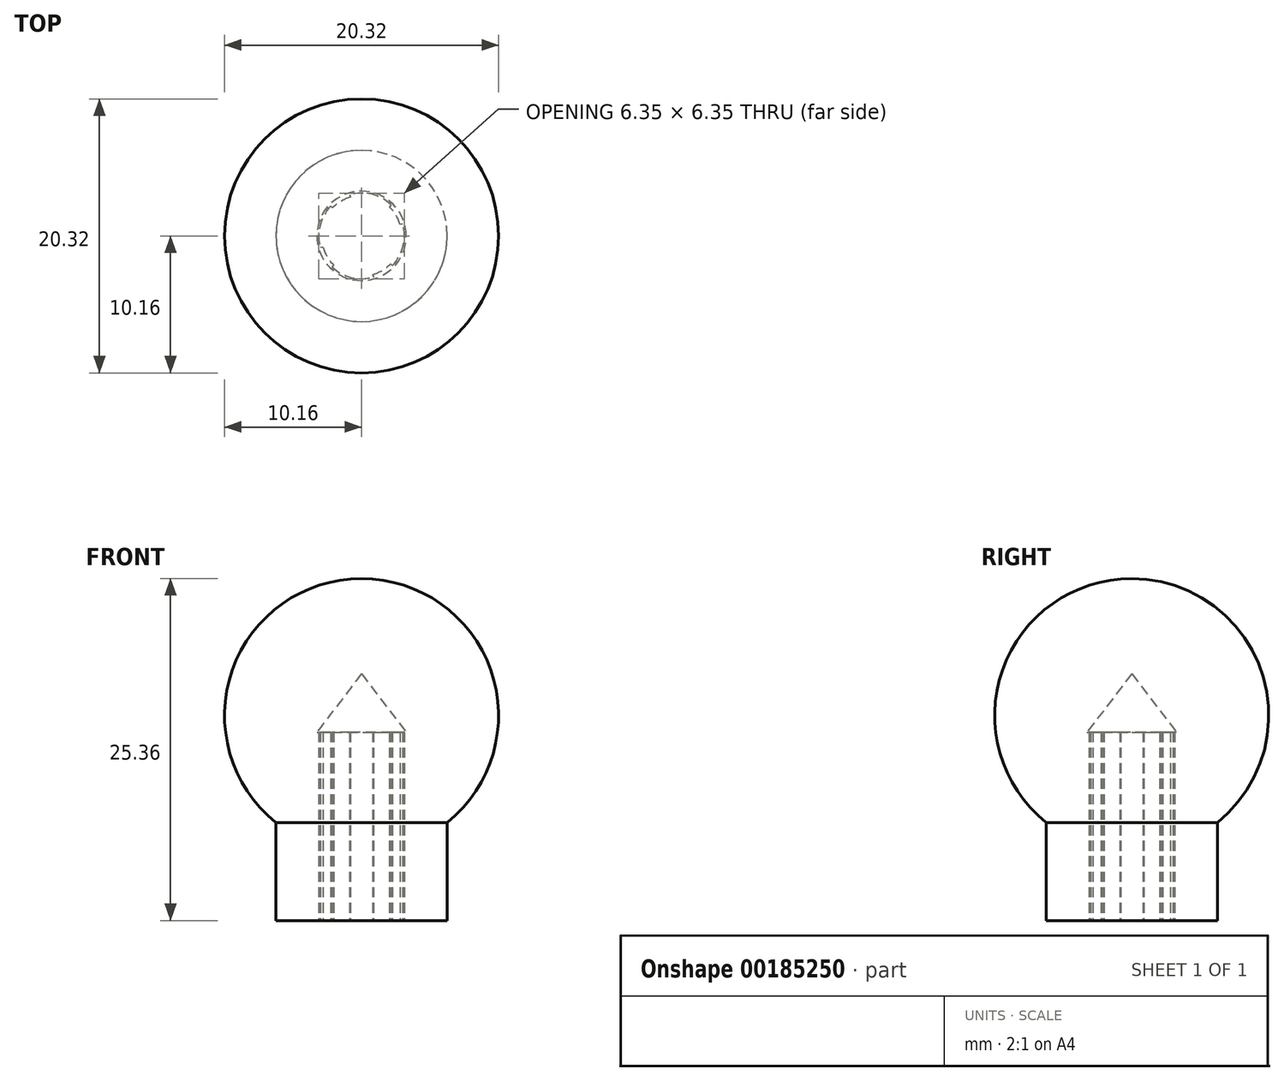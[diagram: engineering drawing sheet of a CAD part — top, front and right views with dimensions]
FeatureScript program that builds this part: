
annotation { "Feature Type Name" : "Feature", "Feature Type Description" : "" }
export const myFeature = defineFeature(function(context is Context, id is Id, definition is map)
    precondition{}
    {
        {
            var Q0;
            Q0=qCreatedBy(makeId("Top.planeOp"),FACE);
            var sketch = newSketch(context, id + "F0", { "sketchPlane" : qUnion([Q0])});
            skArc(sketch, "E0", {"start": v(2.29, -2.2) * mm, "mid": v(3.08, -0.76) * mm, "end": v(3.05, 0.88) * mm});
            skArc(sketch, "E1", {"start": v(-2.87, -0.83) * mm, "mid": v(-2.56, -1.54) * mm, "end": v(-2.07, -2.15) * mm});
            skCircle(sketch, "E2", {"center": v(0, 0) * mm, "radius": 6.35 * mm});
            skLineSegment(sketch, "E3", {"start": v(2.2, 2.29) * mm, "end": v(2.07, 2.15) * mm});
            skLineSegment(sketch, "E4", {"start": v(3.05, 0.88) * mm, "end": v(2.87, 0.83) * mm});
            skLineSegment(sketch, "E5", {"start": v(-2.29, 2.2) * mm, "end": v(-2.15, 2.07) * mm});
            skLineSegment(sketch, "E6", {"start": v(-0.88, 3.05) * mm, "end": v(-0.83, 2.87) * mm});
            skArc(sketch, "E7.trimOffspring", {"start": v(-0.83, 2.87) * mm, "mid": v(-1.54, 2.56) * mm, "end": v(-2.15, 2.07) * mm});
            skArc(sketch, "E8.trimOffspring", {"start": v(2.87, 0.83) * mm, "mid": v(2.56, 1.54) * mm, "end": v(2.07, 2.15) * mm});
            skArc(sketch, "E9.trimOffspring", {"start": v(0.83, -2.87) * mm, "mid": v(1.54, -2.56) * mm, "end": v(2.15, -2.07) * mm});
            skArc(sketch, "E10.trimOffspring", {"start": v(2.2, 2.29) * mm, "mid": v(0.76, 3.08) * mm, "end": v(-0.88, 3.05) * mm});
            skArc(sketch, "E11.trimOffspring", {"start": v(-2.29, 2.2) * mm, "mid": v(-3.08, 0.76) * mm, "end": v(-3.05, -0.88) * mm});
            skArc(sketch, "E12.trimOffspring", {"start": v(-2.2, -2.29) * mm, "mid": v(-0.76, -3.08) * mm, "end": v(0.88, -3.05) * mm});
            skLineSegment(sketch, "E13.trimOffspring", {"start": v(-2.87, -0.83) * mm, "end": v(-3.05, -0.88) * mm});
            skLineSegment(sketch, "E14.trimOffspring", {"start": v(-2.07, -2.15) * mm, "end": v(-2.2, -2.29) * mm});
            skLineSegment(sketch, "E15.trimOffspring", {"start": v(0.83, -2.87) * mm, "end": v(0.88, -3.05) * mm});
            skLineSegment(sketch, "E16.trimOffspring", {"start": v(2.15, -2.07) * mm, "end": v(2.29, -2.2) * mm});
            skSolve(sketch);
        }
        {
            var Q0;
            Q0=makeQuery(id+"F0.imprint","IMPRINT",FACE,{"disambiguationData":[TD([[makeQuery(id+"F0.imprint","IMPRINT",EDGE,{"derivedFrom":sQuery(id+"F0.wireOp",EDGE,"E0")}),-1.0]])]});
            extrude(context, id + "F1", {"entities" : qUnion([Q0]), "depth" : 13.97 * mm});
        }
        {
            var Q0;
            Q0=qCreatedBy(makeId("Right.planeOp"),FACE);
            var sketch = newSketch(context, id + "F2", { "sketchPlane" : qUnion([Q0])});
            skArc(sketch, "E17", {"start": v(4.25, 5.97) * mm, "mid": v(9.92, 17.38) * mm, "end": v(0, 25.36) * mm});
            skLineSegment(sketch, "E18", {"start": v(0, 15.2) * mm, "end": v(0, 25.36) * mm});
            skLineSegment(sketch, "E19", {"start": v(0, 15.2) * mm, "end": v(0, 18.3) * mm});
            skLineSegment(sketch, "E20", {"start": v(4.25, 5.97) * mm, "end": v(3.31, 13.97) * mm});
            skLineSegment(sketch, "E21", {"start": v(3.31, 13.97) * mm, "end": v(0, 18.3) * mm});
            skPoint(sketch, "E22.orphan", {"position": v(0, 5.04) * mm});
            skSolve(sketch);
        }
        {
            var Q0;
            {var subQ0=sQuery(id+"F2.wireOp",EDGE,"E17");Q0=makeQuery(id+"F2.imprint","IMPRINT",FACE,{"disambiguationData":[TD([[makeQuery(id+"F2.imprint","IMPRINT",EDGE,{"derivedFrom":subQ0}),1.0]])]});}
            var Q1;
            Q1=sQuery(id+"F2.wireOp",EDGE,"E19");
            revolve(context, id + "F3", {"operationType" : NewBodyOperationType.ADD, "entities" : qUnion([Q0]), "axis" : qUnion([Q1]), "revolveType" : RevolveType.FULL});
        }
    });
